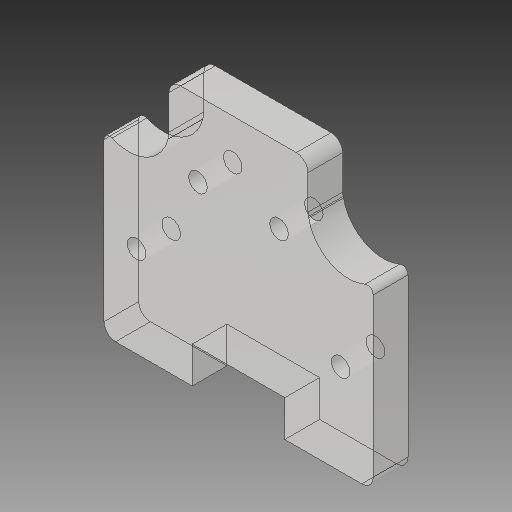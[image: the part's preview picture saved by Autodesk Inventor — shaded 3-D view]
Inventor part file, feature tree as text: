
AUTODESK INVENTOR PART (.ipt)
format: ipt  version: 2017 (Build 210142000, 142)  size: 158,720 bytes
history: native  units: mm
features: sketch x4, other x3, plane x1
ambient origin geometry x8: Origin, YZ Plane, XZ Plane, XY Plane, X Axis, Y Axis, Z Axis, Center Point
bodies: Solid1 (feature_tree)
feature tree (8):
  other  "Hotend Slide Part3_MIR.ipt"
  other  "Solid1::Hotend Slide Part3_MIR.ipt"
  other  "TaggingFeature1"
  sketch  "Sketch1"  dims[d0=10.0mm]
  sketch  "Sketch2"
  sketch  "Sketch3"
  sketch  "Sketch4"
  plane  "Work Plane1"
